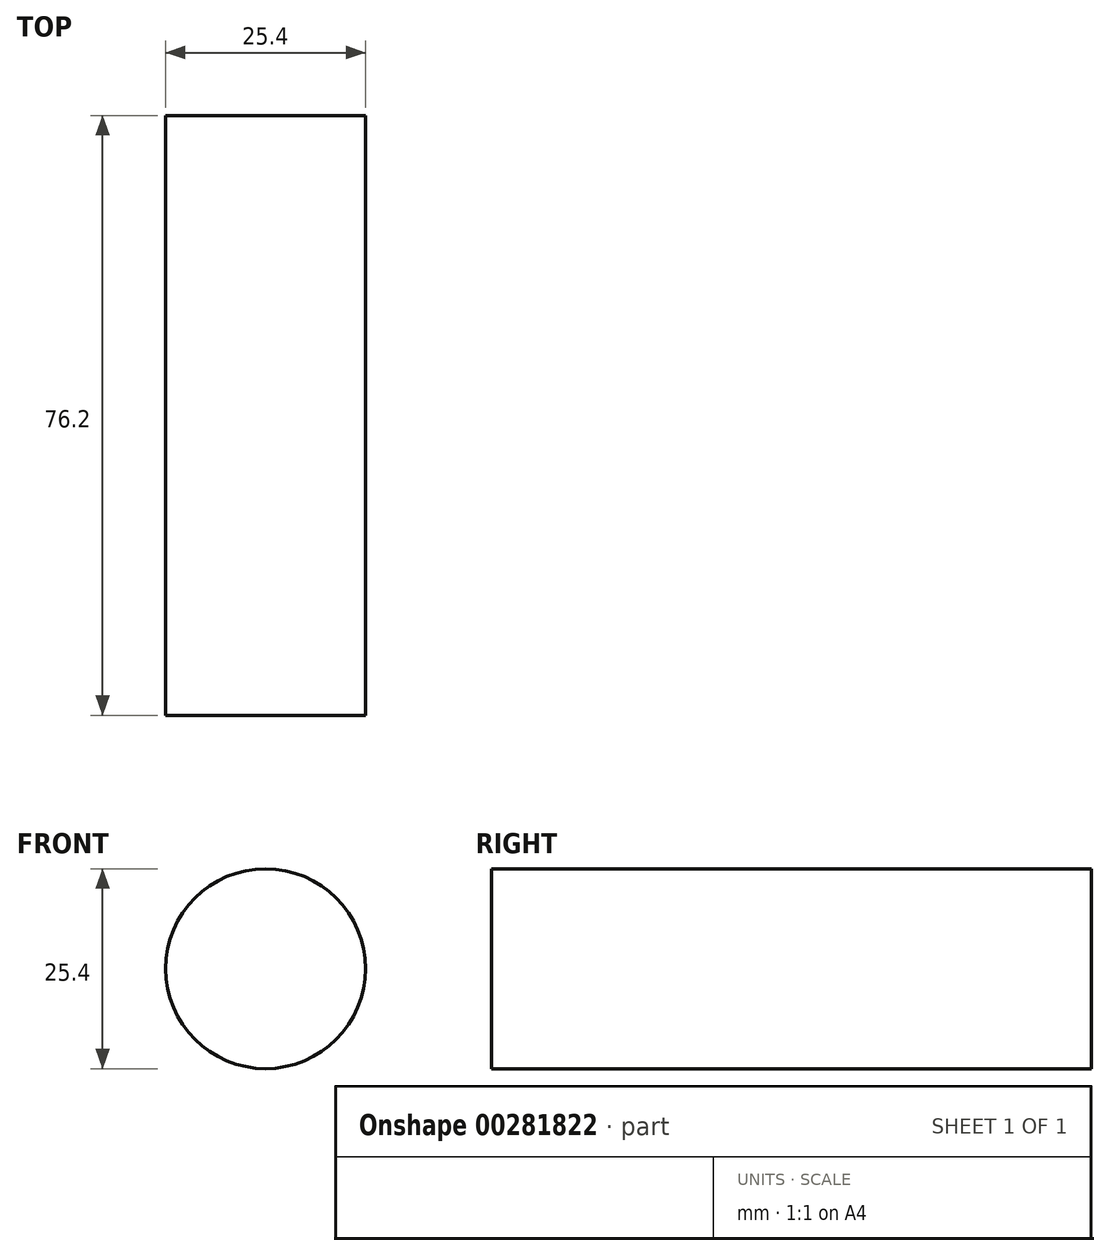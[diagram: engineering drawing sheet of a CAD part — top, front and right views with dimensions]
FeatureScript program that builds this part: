
annotation { "Feature Type Name" : "Feature", "Feature Type Description" : "" }
export const myFeature = defineFeature(function(context is Context, id is Id, definition is map)
    precondition{}
    {
        {
            var Q0;
            Q0=qCreatedBy(makeId("Front.planeOp"),FACE);
            var sketch = newSketch(context, id + "F0", { "sketchPlane" : qUnion([Q0])});
            skCircle(sketch, "E0", {"center": v(-16.23, 12.22) * mm, "radius": 12.7 * mm});
            skSolve(sketch);
        }
        {
            var Q0;
            Q0 = qSketchRegion(id + "F0", true);
            extrude(context, id + "F1", {"entities" : qUnion([Q0]), "depth" : 76.2 * mm});
        }
    });
